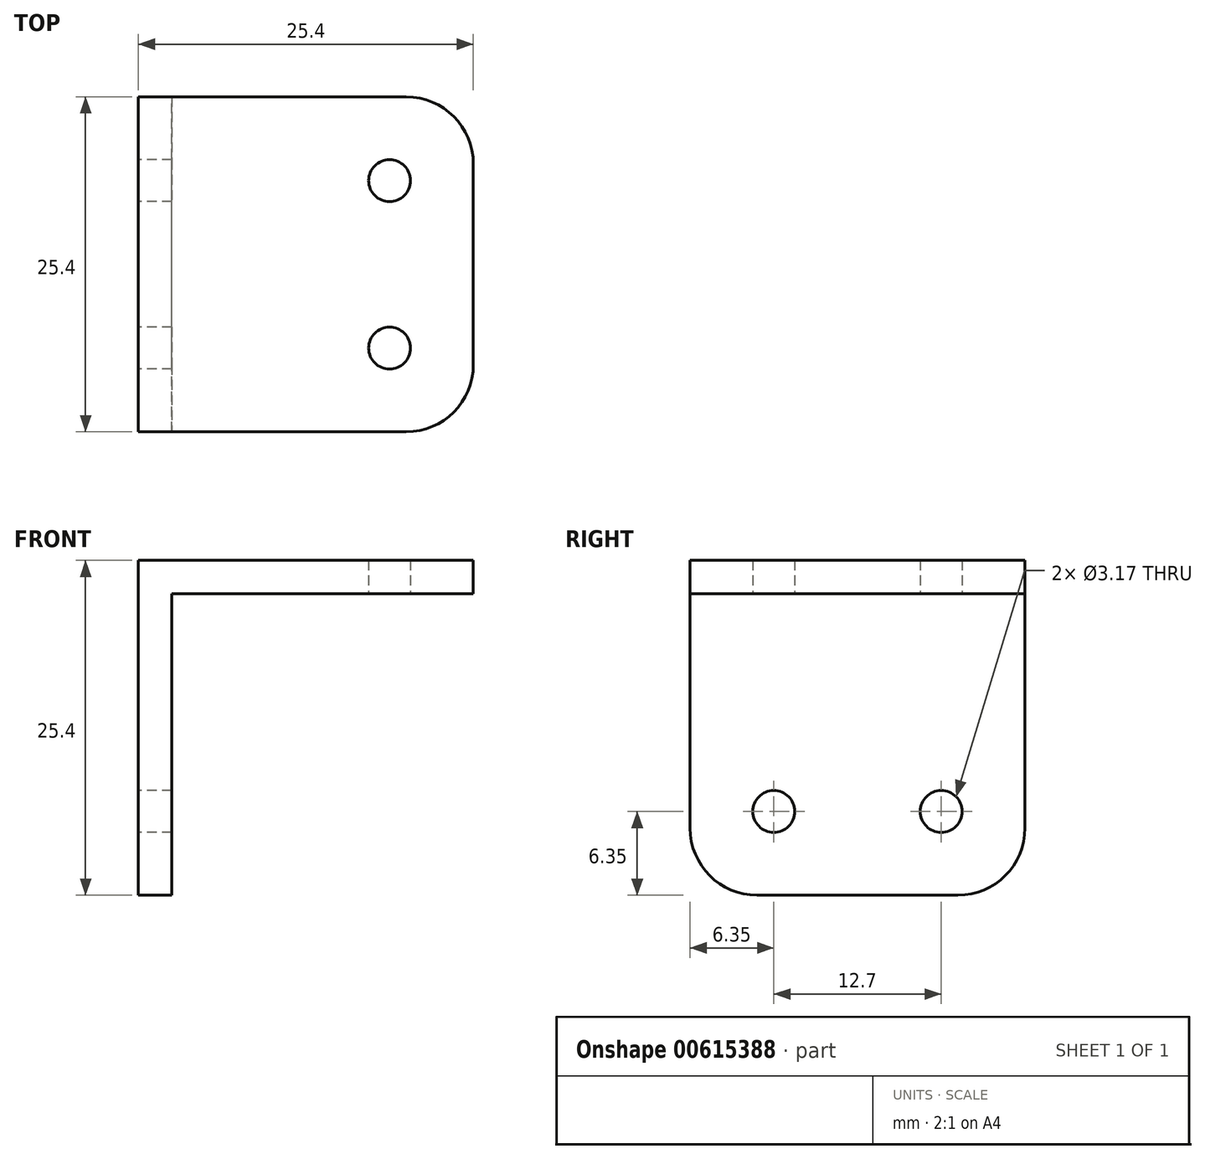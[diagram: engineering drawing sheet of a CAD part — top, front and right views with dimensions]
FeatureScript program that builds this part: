
annotation { "Feature Type Name" : "Feature", "Feature Type Description" : "" }
export const myFeature = defineFeature(function(context is Context, id is Id, definition is map)
    precondition{}
    {
        {
            var Q0;
            Q0=qCreatedBy(makeId("Front.planeOp"),FACE);
            var sketch = newSketch(context, id + "F0", { "sketchPlane" : qUnion([Q0])});
            skLineSegment(sketch, "E0", {"start": v(0, 0) * mm, "end": v(0, 25.4) * mm});
            skLineSegment(sketch, "E1", {"start": v(0, 25.4) * mm, "end": v(25.4, 25.4) * mm});
            skLineSegment(sketch, "E2.0", {"start": v(2.54, 22.86) * mm, "end": v(25.4, 22.86) * mm});
            skLineSegment(sketch, "E2.1", {"start": v(2.54, 0) * mm, "end": v(2.54, 22.86) * mm});
            skLineSegment(sketch, "E3", {"start": v(0, 0) * mm, "end": v(2.54, 0) * mm});
            skLineSegment(sketch, "E4", {"start": v(25.4, 22.86) * mm, "end": v(25.4, 25.4) * mm});
            skSolve(sketch);
        }
        {
            var Q0;
            Q0=qCreatedBy(makeId("Top.planeOp"),FACE);
            var sketch = newSketch(context, id + "F1", { "sketchPlane" : qUnion([Q0])});
            skLineSegment(sketch, "E5", {"start": v(25.4, 0) * mm, "end": v(25.4, -12.7) * mm});
            skLineSegment(sketch, "E6", {"start": v(25.4, -12.7) * mm, "end": v(2.54, -12.7) * mm});
            skLineSegment(sketch, "E7", {"start": v(2.54, -12.7) * mm, "end": v(2.54, 0) * mm});
            skLineSegment(sketch, "E8.MirrorCS", {"start": v(25.4, 12.7) * mm, "end": v(2.54, 12.7) * mm});
            skLineSegment(sketch, "E9.MirrorCS", {"start": v(2.54, 12.7) * mm, "end": v(2.54, 0) * mm});
            skLineSegment(sketch, "E10.MirrorCS", {"start": v(25.4, 0) * mm, "end": v(25.4, 12.7) * mm});
            skLineSegment(sketch, "E11", {"start": v(25.4, 0) * mm, "end": v(19.05, 0) * mm});
            skLineSegment(sketch, "E12.0", {"start": v(25.4, 6.35) * mm, "end": v(19.05, 6.35) * mm});
            skLineSegment(sketch, "E13.0", {"start": v(25.4, -6.35) * mm, "end": v(19.05, -6.35) * mm});
            skCircle(sketch, "E14", {"center": v(19.05, -6.35) * mm, "radius": 1.59 * mm});
            skCircle(sketch, "E15", {"center": v(19.05, 6.35) * mm, "radius": 1.59 * mm});
            skSolve(sketch);
        }
        {
            var Q0;
            Q0=qCreatedBy(makeId("Right.planeOp"),FACE);
            var sketch = newSketch(context, id + "F2", { "sketchPlane" : qUnion([Q0])});
            skLineSegment(sketch, "E16", {"start": v(0, 0) * mm, "end": v(-12.7, 0) * mm});
            skLineSegment(sketch, "E17", {"start": v(-12.7, 0) * mm, "end": v(-12.7, 25.4) * mm});
            skLineSegment(sketch, "E18", {"start": v(-12.7, 25.4) * mm, "end": v(0, 25.4) * mm});
            skLineSegment(sketch, "E19.MirrorCS", {"start": v(12.7, 25.4) * mm, "end": v(0, 25.4) * mm});
            skLineSegment(sketch, "E20.MirrorCS", {"start": v(12.7, 0) * mm, "end": v(12.7, 25.4) * mm});
            skLineSegment(sketch, "E21.MirrorCS", {"start": v(0, 0) * mm, "end": v(12.7, 0) * mm});
            skLineSegment(sketch, "E22.0", {"start": v(6.35, 0) * mm, "end": v(6.35, 6.35) * mm});
            skLineSegment(sketch, "E23.0", {"start": v(-6.35, 0) * mm, "end": v(-6.35, 6.35) * mm});
            skPoint(sketch, "E24.orphan", {"position": v(0, 22.86) * mm});
            skCircle(sketch, "E25", {"center": v(-6.35, 6.35) * mm, "radius": 1.59 * mm});
            skCircle(sketch, "E26", {"center": v(6.35, 6.35) * mm, "radius": 1.59 * mm});
            skSolve(sketch);
        }
        {
            var Q0;
            Q0=makeQuery(id+"F0.imprint","IMPRINT",FACE,{"disambiguationData":[TD([[makeQuery(id+"F0.imprint","IMPRINT",EDGE,{"derivedFrom":sQuery(id+"F0.wireOp",EDGE,"E0")}),-1.0]])]});
            extrude(context, id + "F3", {"entities" : qUnion([Q0]), "endBound" : BoundingType.SYMMETRIC, "depth" : 25.4 * mm, "offsetDistance" : 25.4 * mm});
        }
        {
            var Q0;
            Q0=makeQuery(id+"F1.imprint","IMPRINT",FACE,{"disambiguationData":[TD([[makeQuery(id+"F1.imprint","IMPRINT",EDGE,{"derivedFrom":sQuery(id+"F1.wireOp",EDGE,"E15")}),1.0]])]});
            var Q1;
            Q1=makeQuery(id+"F1.imprint","IMPRINT",FACE,{"disambiguationData":[TD([[makeQuery(id+"F1.imprint","IMPRINT",EDGE,{"derivedFrom":sQuery(id+"F1.wireOp",EDGE,"E14")}),1.0]])]});
            extrude(context, id + "F4", {"entities" : qUnion([Q0, Q1]), "operationType" : NewBodyOperationType.REMOVE, "depth" : 39.37 * mm, "offsetDistance" : 25.4 * mm});
        }
        {
            var Q0;
            Q0=makeQuery(id+"F2.imprint","IMPRINT",FACE,{"disambiguationData":[TD([[makeQuery(id+"F2.imprint","IMPRINT",EDGE,{"derivedFrom":sQuery(id+"F2.wireOp",EDGE,"E26")}),1.0]])]});
            var Q1;
            Q1=makeQuery(id+"F2.imprint","IMPRINT",FACE,{"disambiguationData":[TD([[makeQuery(id+"F2.imprint","IMPRINT",EDGE,{"derivedFrom":sQuery(id+"F2.wireOp",EDGE,"E25")}),1.0]])]});
            extrude(context, id + "F5", {"entities" : qUnion([Q0, Q1]), "operationType" : NewBodyOperationType.REMOVE, "depth" : 8.38 * mm, "offsetDistance" : 25.4 * mm});
        }
        {
            var Q0;
            Q0=makeQuery(id+"F3.opExtrude","CAP_EDGE",EDGE,{"disambiguationData":[OSD([sQuery(id+"F0.wireOp",EDGE,"E4")])],"isStart":false});
            var Q1;
            Q1=makeQuery(id+"F3.opExtrude","CAP_EDGE",EDGE,{"disambiguationData":[OSD([sQuery(id+"F0.wireOp",EDGE,"E4")])],"isStart":true});
            var Q2;
            Q2=makeQuery(id+"F3.opExtrude","CAP_EDGE",EDGE,{"disambiguationData":[OSD([sQuery(id+"F0.wireOp",EDGE,"E3")])],"isStart":false});
            var Q3;
            Q3=makeQuery(id+"F3.opExtrude","CAP_EDGE",EDGE,{"disambiguationData":[OSD([sQuery(id+"F0.wireOp",EDGE,"E3")])],"isStart":true});
            fillet(context, id + "F6", {"entities" : qUnion([Q0, Q1, Q2, Q3]), "radius" : 5.08 * mm, "tangentPropagation" : true, "allowEdgeOverflow" : false});
        }
    });
